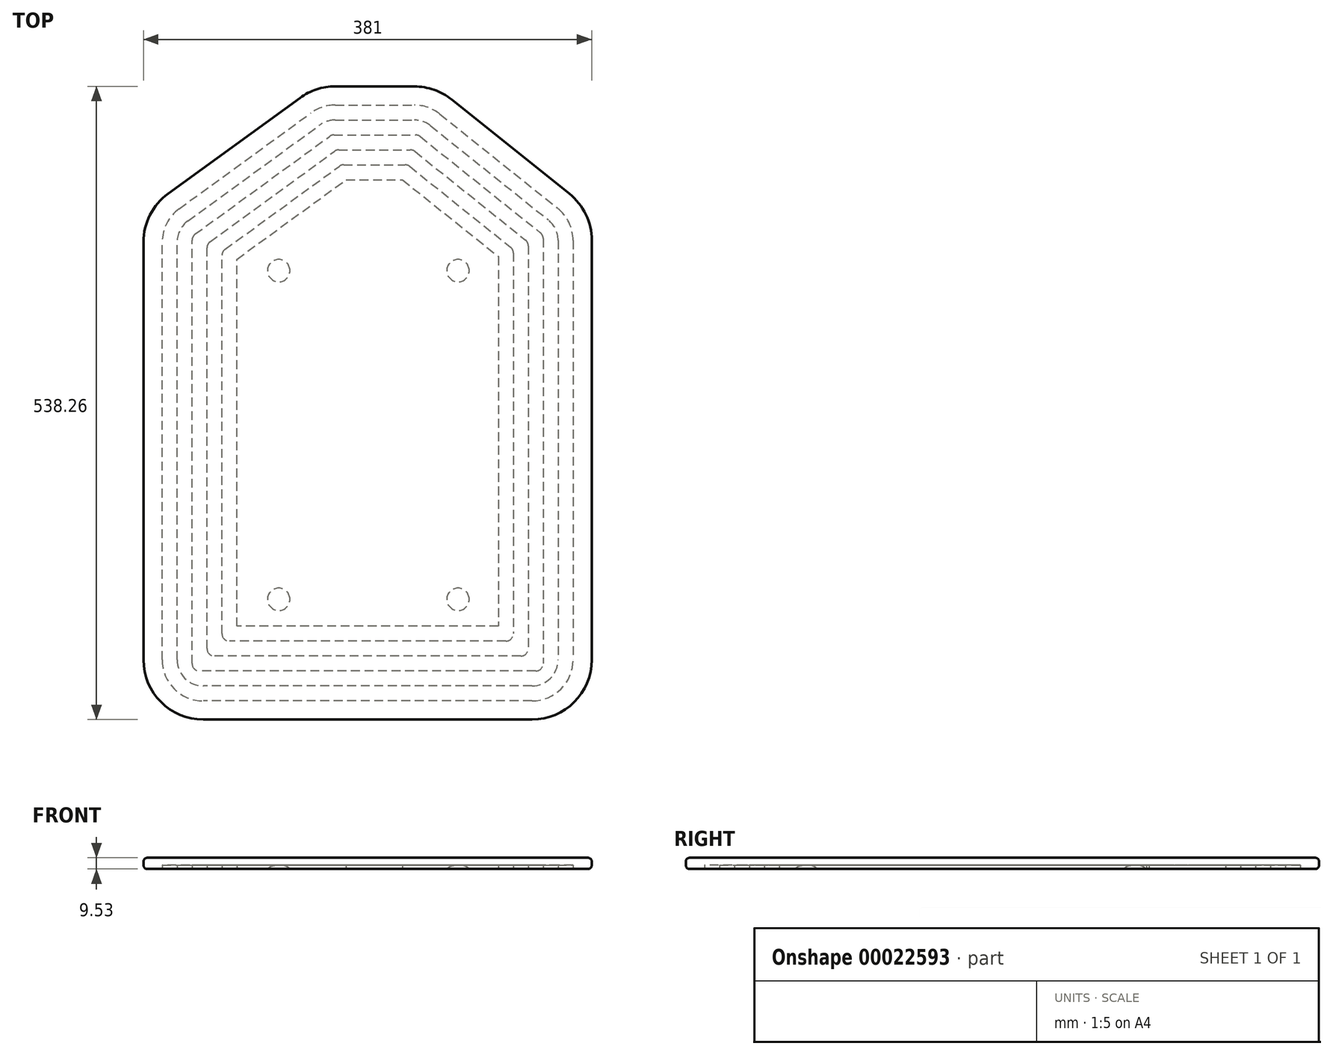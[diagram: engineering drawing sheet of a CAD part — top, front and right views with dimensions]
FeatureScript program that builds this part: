
annotation { "Feature Type Name" : "Feature", "Feature Type Description" : "" }
export const myFeature = defineFeature(function(context is Context, id is Id, definition is map)
    precondition{}
    {
        {
            var Q0;
            Q0=qCreatedBy(makeId("Top.planeOp"),FACE);
            var sketch = newSketch(context, id + "F0", { "sketchPlane" : qUnion([Q0])});
            skLineSegment(sketch, "E0.bottom", {"start": v(138.95, -254.97) * mm, "end": v(-140.45, -254.97) * mm});
            skLineSegment(sketch, "E0.left", {"start": v(189.75, -204.17) * mm, "end": v(189.75, 152.42) * mm});
            skLineSegment(sketch, "E0.right", {"start": v(-191.25, -204.17) * mm, "end": v(-191.25, 150.96) * mm});
            skPoint(sketch, "E0.middle", {"position": v(-0.75, -39.07) * mm});
            skLineSegment(sketch, "E1.bottom", {"start": v(38.9, 283.3) * mm, "end": v(-28.35, 283.3) * mm});
            skPoint(sketch, "E1.middle", {"position": v(-0.75, 176.83) * mm});
            skLineSegment(sketch, "E2", {"start": v(-58.23, 273.57) * mm, "end": v(-170.33, 192.05) * mm});
            skLineSegment(sketch, "E3", {"start": v(170.7, 192.08) * mm, "end": v(70.65, 272.15) * mm});
            skPoint(sketch, "E4.orphan", {"position": v(-58.23, 70.37) * mm});
            skPoint(sketch, "E5.orphan", {"position": v(43.37, 70.37) * mm});
            skPoint(sketch, "E6.visualSharp", {"position": v(-44.87, 283.3) * mm});
            skArc(sketch, "E6.filletArc", {"start": v(-28.35, 283.3) * mm, "mid": v(-44.06, 280.8) * mm, "end": v(-58.23, 273.57) * mm});
            skPoint(sketch, "E7.visualSharp", {"position": v(56.73, 283.3) * mm});
            skArc(sketch, "E7.filletArc", {"start": v(70.65, 272.15) * mm, "mid": v(55.72, 280.43) * mm, "end": v(38.9, 283.3) * mm});
            skPoint(sketch, "E8.visualSharp", {"position": v(189.75, 176.83) * mm});
            skArc(sketch, "E8.filletArc", {"start": v(189.75, 152.42) * mm, "mid": v(184.74, 174.42) * mm, "end": v(170.7, 192.08) * mm});
            skPoint(sketch, "E9.visualSharp", {"position": v(189.75, -254.97) * mm});
            skArc(sketch, "E9.filletArc", {"start": v(138.95, -254.97) * mm, "mid": v(174.87, -240.09) * mm, "end": v(189.75, -204.17) * mm});
            skPoint(sketch, "E10.visualSharp", {"position": v(-191.25, -254.97) * mm});
            skArc(sketch, "E10.filletArc", {"start": v(-191.25, -204.17) * mm, "mid": v(-176.37, -240.09) * mm, "end": v(-140.45, -254.97) * mm});
            skPoint(sketch, "E11.visualSharp", {"position": v(-191.25, 176.83) * mm});
            skArc(sketch, "E11.filletArc", {"start": v(-170.33, 192.05) * mm, "mid": v(-185.72, 174.02) * mm, "end": v(-191.25, 150.96) * mm});
            skSolve(sketch);
        }
        {
            var Q0;
            Q0=makeQuery(id+"F0.imprint","IMPRINT",FACE,{"disambiguationData":[TD([[makeQuery(id+"F0.imprint","IMPRINT",EDGE,{"derivedFrom":sQuery(id+"F0.wireOp",EDGE,"E0.bottom")}),-1.0]])]});
            extrude(context, id + "F1", {"entities" : qUnion([Q0]), "depth" : 9.52 * mm});
        }
        {
            var Q0;
            Q0=makeQuery(id+"F1.opExtrude","CAP_EDGE",EDGE,{"disambiguationData":[OSD([sQuery(id+"F0.wireOp",EDGE,"E10.filletArc")])],"isStart":false});
            var Q1;
            Q1=makeQuery(id+"F1.opExtrude","CAP_EDGE",EDGE,{"disambiguationData":[OSD([sQuery(id+"F0.wireOp",EDGE,"E0.right")])],"isStart":false});
            var Q2;
            Q2=makeQuery(id+"F1.opExtrude","CAP_EDGE",EDGE,{"disambiguationData":[OSD([sQuery(id+"F0.wireOp",EDGE,"E11.filletArc")])],"isStart":false});
            var Q3;
            Q3=makeQuery(id+"F1.opExtrude","CAP_EDGE",EDGE,{"disambiguationData":[OSD([sQuery(id+"F0.wireOp",EDGE,"E2")])],"isStart":false});
            var Q4;
            Q4=makeQuery(id+"F1.opExtrude","CAP_EDGE",EDGE,{"disambiguationData":[OSD([sQuery(id+"F0.wireOp",EDGE,"E1.bottom")])],"isStart":false});
            var Q5;
            Q5=makeQuery(id+"F1.opExtrude","CAP_EDGE",EDGE,{"disambiguationData":[OSD([sQuery(id+"F0.wireOp",EDGE,"E6.filletArc")])],"isStart":false});
            var Q6;
            Q6=makeQuery(id+"F1.opExtrude","CAP_EDGE",EDGE,{"disambiguationData":[OSD([sQuery(id+"F0.wireOp",EDGE,"E3")])],"isStart":false});
            var Q7;
            Q7=makeQuery(id+"F1.opExtrude","CAP_EDGE",EDGE,{"disambiguationData":[OSD([sQuery(id+"F0.wireOp",EDGE,"E7.filletArc")])],"isStart":false});
            var Q8;
            Q8=makeQuery(id+"F1.opExtrude","CAP_EDGE",EDGE,{"disambiguationData":[OSD([sQuery(id+"F0.wireOp",EDGE,"E0.left")])],"isStart":false});
            var Q9;
            Q9=makeQuery(id+"F1.opExtrude","CAP_EDGE",EDGE,{"disambiguationData":[OSD([sQuery(id+"F0.wireOp",EDGE,"E8.filletArc")])],"isStart":false});
            var Q10;
            Q10=makeQuery(id+"F1.opExtrude","CAP_EDGE",EDGE,{"disambiguationData":[OSD([sQuery(id+"F0.wireOp",EDGE,"E9.filletArc")])],"isStart":false});
            var Q11;
            Q11=makeQuery(id+"F1.opExtrude","CAP_EDGE",EDGE,{"disambiguationData":[OSD([sQuery(id+"F0.wireOp",EDGE,"E0.bottom")])],"isStart":false});
            fillet(context, id + "F2", {"entities" : qUnion([Q0, Q1, Q2, Q3, Q4, Q5, Q6, Q7, Q8, Q9, Q10, Q11]), "radius" : 3.17 * mm, "tangentPropagation" : true, "allowEdgeOverflow" : false});
        }
        {
            var Q0;
            Q0=makeQuery(id+"F1.opExtrude","CAP_EDGE",EDGE,{"disambiguationData":[OSD([sQuery(id+"F0.wireOp",EDGE,"E0.bottom")])],"isStart":true});
            var Q1;
            Q1=makeQuery(id+"F1.opExtrude","CAP_EDGE",EDGE,{"disambiguationData":[OSD([sQuery(id+"F0.wireOp",EDGE,"E0.right")])],"isStart":true});
            var Q2;
            Q2=makeQuery(id+"F1.opExtrude","CAP_EDGE",EDGE,{"disambiguationData":[OSD([sQuery(id+"F0.wireOp",EDGE,"E10.filletArc")])],"isStart":true});
            var Q3;
            Q3=makeQuery(id+"F1.opExtrude","CAP_EDGE",EDGE,{"disambiguationData":[OSD([sQuery(id+"F0.wireOp",EDGE,"E9.filletArc")])],"isStart":true});
            var Q4;
            Q4=makeQuery(id+"F1.opExtrude","CAP_EDGE",EDGE,{"disambiguationData":[OSD([sQuery(id+"F0.wireOp",EDGE,"E0.left")])],"isStart":true});
            var Q5;
            Q5=makeQuery(id+"F1.opExtrude","CAP_EDGE",EDGE,{"disambiguationData":[OSD([sQuery(id+"F0.wireOp",EDGE,"E8.filletArc")])],"isStart":true});
            var Q6;
            Q6=makeQuery(id+"F1.opExtrude","CAP_EDGE",EDGE,{"disambiguationData":[OSD([sQuery(id+"F0.wireOp",EDGE,"E3")])],"isStart":true});
            var Q7;
            Q7=makeQuery(id+"F1.opExtrude","CAP_EDGE",EDGE,{"disambiguationData":[OSD([sQuery(id+"F0.wireOp",EDGE,"E7.filletArc")])],"isStart":true});
            var Q8;
            Q8=makeQuery(id+"F1.opExtrude","CAP_EDGE",EDGE,{"disambiguationData":[OSD([sQuery(id+"F0.wireOp",EDGE,"E1.bottom")])],"isStart":true});
            var Q9;
            Q9=makeQuery(id+"F1.opExtrude","CAP_EDGE",EDGE,{"disambiguationData":[OSD([sQuery(id+"F0.wireOp",EDGE,"E6.filletArc")])],"isStart":true});
            var Q10;
            Q10=makeQuery(id+"F1.opExtrude","CAP_EDGE",EDGE,{"disambiguationData":[OSD([sQuery(id+"F0.wireOp",EDGE,"E2")])],"isStart":true});
            var Q11;
            Q11=makeQuery(id+"F1.opExtrude","CAP_EDGE",EDGE,{"disambiguationData":[OSD([sQuery(id+"F0.wireOp",EDGE,"E11.filletArc")])],"isStart":true});
            fillet(context, id + "F3", {"entities" : qUnion([Q0, Q1, Q2, Q3, Q4, Q5, Q6, Q7, Q8, Q9, Q10, Q11]), "radius" : 3.17 * mm, "tangentPropagation" : true, "allowEdgeOverflow" : false});
        }
        {
            var Q0;
            Q0=makeQuery(id+"F1.opExtrude","CAP_FACE",FACE,{"disambiguationData":[OSD([sQuery(id+"F0.wireOp",EDGE,"E0.bottom"),sQuery(id+"F0.wireOp",EDGE,"E0.left"),sQuery(id+"F0.wireOp",EDGE,"E0.right"),sQuery(id+"F0.wireOp",EDGE,"E1.bottom"),sQuery(id+"F0.wireOp",EDGE,"E2"),sQuery(id+"F0.wireOp",EDGE,"E3"),sQuery(id+"F0.wireOp",EDGE,"E6.filletArc"),sQuery(id+"F0.wireOp",EDGE,"E7.filletArc"),sQuery(id+"F0.wireOp",EDGE,"E8.filletArc"),sQuery(id+"F0.wireOp",EDGE,"E9.filletArc"),sQuery(id+"F0.wireOp",EDGE,"E10.filletArc"),sQuery(id+"F0.wireOp",EDGE,"E11.filletArc")])],"isStart":true});
            var sketch = newSketch(context, id + "F4", { "sketchPlane" : qUnion([Q0])});
            skArc(sketch, "E12.0", {"start": v(38.9, -267.42) * mm, "mid": v(50.47, -265.45) * mm, "end": v(60.73, -259.76) * mm});
            skLineSegment(sketch, "E12.1", {"start": v(138.95, 239.1) * mm, "end": v(-140.45, 239.1) * mm});
            skArc(sketch, "E12.2", {"start": v(173.87, 204.17) * mm, "mid": v(163.65, 228.86) * mm, "end": v(138.95, 239.1) * mm});
            skLineSegment(sketch, "E12.3", {"start": v(173.87, -152.42) * mm, "end": v(173.87, 204.17) * mm});
            skArc(sketch, "E12.4", {"start": v(160.77, -179.7) * mm, "mid": v(170.43, -167.55) * mm, "end": v(173.87, -152.42) * mm});
            skArc(sketch, "E12.5", {"start": v(-140.45, 239.1) * mm, "mid": v(-165.15, 228.86) * mm, "end": v(-175.38, 204.17) * mm});
            skLineSegment(sketch, "E12.6", {"start": v(60.73, -259.76) * mm, "end": v(160.77, -179.7) * mm});
            skLineSegment(sketch, "E12.7", {"start": v(-175.38, 204.17) * mm, "end": v(-175.38, -150.96) * mm});
            skArc(sketch, "E12.8", {"start": v(-175.38, -150.96) * mm, "mid": v(-171.57, -166.81) * mm, "end": v(-161, -179.2) * mm});
            skLineSegment(sketch, "E12.9", {"start": v(-161, -179.2) * mm, "end": v(-48.9, -260.74) * mm});
            skArc(sketch, "E12.10", {"start": v(-48.9, -260.74) * mm, "mid": v(-39.15, -265.7) * mm, "end": v(-28.35, -267.42) * mm});
            skLineSegment(sketch, "E12.11", {"start": v(-28.35, -267.42) * mm, "end": v(38.9, -267.42) * mm});
            skLineSegment(sketch, "E13.0", {"start": v(138.95, 226.4) * mm, "end": v(-140.45, 226.4) * mm});
            skArc(sketch, "E13.1", {"start": v(-41.42, -250.46) * mm, "mid": v(-35.22, -253.63) * mm, "end": v(-28.35, -254.72) * mm});
            skLineSegment(sketch, "E13.2", {"start": v(-153.52, -168.94) * mm, "end": v(-41.42, -250.46) * mm});
            skArc(sketch, "E13.3", {"start": v(-162.68, -150.96) * mm, "mid": v(-160.26, -161.05) * mm, "end": v(-153.52, -168.94) * mm});
            skLineSegment(sketch, "E13.4", {"start": v(-162.68, 204.17) * mm, "end": v(-162.68, -150.96) * mm});
            skLineSegment(sketch, "E13.5", {"start": v(-28.35, -254.72) * mm, "end": v(38.9, -254.72) * mm});
            skArc(sketch, "E13.6", {"start": v(-140.45, 226.4) * mm, "mid": v(-156.17, 219.88) * mm, "end": v(-162.68, 204.17) * mm});
            skArc(sketch, "E13.7", {"start": v(38.9, -254.72) * mm, "mid": v(46.26, -253.46) * mm, "end": v(52.8, -249.84) * mm});
            skLineSegment(sketch, "E13.8", {"start": v(52.8, -249.84) * mm, "end": v(152.84, -169.77) * mm});
            skArc(sketch, "E13.9", {"start": v(152.84, -169.77) * mm, "mid": v(158.98, -162.05) * mm, "end": v(161.17, -152.42) * mm});
            skLineSegment(sketch, "E13.10", {"start": v(161.17, -152.42) * mm, "end": v(161.17, 204.17) * mm});
            skArc(sketch, "E13.11", {"start": v(161.17, 204.17) * mm, "mid": v(154.67, 219.88) * mm, "end": v(138.95, 226.4) * mm});
            skLineSegment(sketch, "E14.0", {"start": v(148.47, -153.95) * mm, "end": v(148.47, 207.34) * mm});
            skLineSegment(sketch, "E14.1", {"start": v(-149.98, 207.34) * mm, "end": v(-149.98, -152.58) * mm});
            skLineSegment(sketch, "E14.2", {"start": v(-147.36, -157.72) * mm, "end": v(-33.12, -240.8) * mm});
            skLineSegment(sketch, "E14.3", {"start": v(142.12, 213.7) * mm, "end": v(-143.63, 213.7) * mm});
            skLineSegment(sketch, "E14.4", {"start": v(-29.38, -242.02) * mm, "end": v(40.02, -242.02) * mm});
            skLineSegment(sketch, "E14.5", {"start": v(43.99, -240.62) * mm, "end": v(146.1, -158.9) * mm});
            skLineSegment(sketch, "E15.0", {"start": v(135.77, -147.85) * mm, "end": v(135.77, 194.64) * mm});
            skLineSegment(sketch, "E15.1", {"start": v(-137.28, 194.64) * mm, "end": v(-137.28, -146.11) * mm});
            skLineSegment(sketch, "E15.2", {"start": v(-134.66, -151.25) * mm, "end": v(-28.99, -228.1) * mm});
            skLineSegment(sketch, "E15.3", {"start": v(129.42, 201) * mm, "end": v(-130.93, 201) * mm});
            skLineSegment(sketch, "E15.4", {"start": v(-25.25, -229.32) * mm, "end": v(35.56, -229.32) * mm});
            skLineSegment(sketch, "E15.5", {"start": v(39.53, -227.92) * mm, "end": v(133.4, -152.8) * mm});
            skLineSegment(sketch, "E16.0", {"start": v(116.72, 188.3) * mm, "end": v(-118.23, 188.3) * mm});
            skLineSegment(sketch, "E16.1", {"start": v(-121.96, -144.78) * mm, "end": v(-24.86, -215.4) * mm});
            skLineSegment(sketch, "E16.2", {"start": v(-21.12, -216.62) * mm, "end": v(31.1, -216.62) * mm});
            skLineSegment(sketch, "E16.3", {"start": v(-124.58, 181.94) * mm, "end": v(-124.58, -139.65) * mm});
            skLineSegment(sketch, "E16.4", {"start": v(35.07, -215.22) * mm, "end": v(120.7, -146.7) * mm});
            skLineSegment(sketch, "E16.5", {"start": v(123.07, -141.74) * mm, "end": v(123.07, 181.94) * mm});
            skLineSegment(sketch, "E17.bottom", {"start": v(95.6, -133.68) * mm, "end": v(-94.9, -133.68) * mm});
            skLineSegment(sketch, "E17.top", {"start": v(95.6, 158.42) * mm, "end": v(-94.9, 158.42) * mm});
            skLineSegment(sketch, "E17.left", {"start": v(95.6, -133.68) * mm, "end": v(95.6, 158.42) * mm});
            skLineSegment(sketch, "E17.right", {"start": v(-94.9, -133.68) * mm, "end": v(-94.9, 158.42) * mm});
            skPoint(sketch, "E17.middle", {"position": v(0.35, 12.37) * mm});
            skPoint(sketch, "E18.visualSharp", {"position": v(-137.28, 201) * mm});
            skArc(sketch, "E18.filletArc", {"start": v(-130.93, 201) * mm, "mid": v(-135.42, 199.13) * mm, "end": v(-137.28, 194.64) * mm});
            skPoint(sketch, "E19.visualSharp", {"position": v(-149.98, 213.7) * mm});
            skArc(sketch, "E19.filletArc", {"start": v(-143.63, 213.7) * mm, "mid": v(-148.12, 211.83) * mm, "end": v(-149.98, 207.34) * mm});
            skPoint(sketch, "E20.visualSharp", {"position": v(-124.58, 188.3) * mm});
            skArc(sketch, "E20.filletArc", {"start": v(-118.23, 188.3) * mm, "mid": v(-122.72, 186.43) * mm, "end": v(-124.58, 181.94) * mm});
            skPoint(sketch, "E21.visualSharp", {"position": v(148.47, 213.7) * mm});
            skArc(sketch, "E21.filletArc", {"start": v(148.47, 207.34) * mm, "mid": v(146.61, 211.83) * mm, "end": v(142.12, 213.7) * mm});
            skPoint(sketch, "E22.visualSharp", {"position": v(135.77, 201) * mm});
            skArc(sketch, "E22.filletArc", {"start": v(135.77, 194.64) * mm, "mid": v(133.91, 199.13) * mm, "end": v(129.42, 201) * mm});
            skPoint(sketch, "E23.visualSharp", {"position": v(123.07, 188.3) * mm});
            skArc(sketch, "E23.filletArc", {"start": v(123.07, 181.94) * mm, "mid": v(121.21, 186.43) * mm, "end": v(116.72, 188.3) * mm});
            skPoint(sketch, "E24.visualSharp", {"position": v(-149.98, -155.81) * mm});
            skArc(sketch, "E24.filletArc", {"start": v(-149.98, -152.58) * mm, "mid": v(-149.28, -155.46) * mm, "end": v(-147.36, -157.72) * mm});
            skPoint(sketch, "E25.visualSharp", {"position": v(-137.28, -149.35) * mm});
            skArc(sketch, "E25.filletArc", {"start": v(-137.28, -146.11) * mm, "mid": v(-136.58, -149) * mm, "end": v(-134.66, -151.25) * mm});
            skPoint(sketch, "E26.visualSharp", {"position": v(-124.58, -142.88) * mm});
            skArc(sketch, "E26.filletArc", {"start": v(-124.58, -139.65) * mm, "mid": v(-123.88, -142.53) * mm, "end": v(-121.96, -144.78) * mm});
            skPoint(sketch, "E27.visualSharp", {"position": v(148.47, -157) * mm});
            skArc(sketch, "E27.filletArc", {"start": v(146.1, -158.9) * mm, "mid": v(147.85, -156.7) * mm, "end": v(148.47, -153.95) * mm});
            skPoint(sketch, "E28.visualSharp", {"position": v(135.77, -150.9) * mm});
            skArc(sketch, "E28.filletArc", {"start": v(133.4, -152.8) * mm, "mid": v(135.15, -150.6) * mm, "end": v(135.77, -147.85) * mm});
            skPoint(sketch, "E29.visualSharp", {"position": v(123.07, -144.8) * mm});
            skArc(sketch, "E29.filletArc", {"start": v(120.7, -146.7) * mm, "mid": v(122.45, -144.5) * mm, "end": v(123.07, -141.74) * mm});
            skPoint(sketch, "E30.visualSharp", {"position": v(-31.45, -242.02) * mm});
            skArc(sketch, "E30.filletArc", {"start": v(-33.12, -240.8) * mm, "mid": v(-31.35, -241.7) * mm, "end": v(-29.38, -242.02) * mm});
            skPoint(sketch, "E31.visualSharp", {"position": v(42.25, -242.02) * mm});
            skArc(sketch, "E31.filletArc", {"start": v(40.02, -242.02) * mm, "mid": v(42.12, -241.66) * mm, "end": v(43.99, -240.62) * mm});
            skPoint(sketch, "E32.visualSharp", {"position": v(37.8, -229.32) * mm});
            skArc(sketch, "E32.filletArc", {"start": v(35.56, -229.32) * mm, "mid": v(37.66, -228.96) * mm, "end": v(39.53, -227.92) * mm});
            skPoint(sketch, "E33.visualSharp", {"position": v(33.33, -216.62) * mm});
            skArc(sketch, "E33.filletArc", {"start": v(31.1, -216.62) * mm, "mid": v(33.2, -216.26) * mm, "end": v(35.07, -215.22) * mm});
            skPoint(sketch, "E34.visualSharp", {"position": v(-23.19, -216.62) * mm});
            skArc(sketch, "E34.filletArc", {"start": v(-24.86, -215.4) * mm, "mid": v(-23.09, -216.3) * mm, "end": v(-21.12, -216.62) * mm});
            skPoint(sketch, "E35.visualSharp", {"position": v(-27.32, -229.32) * mm});
            skArc(sketch, "E35.filletArc", {"start": v(-28.99, -228.1) * mm, "mid": v(-27.22, -229) * mm, "end": v(-25.25, -229.32) * mm});
            skLineSegment(sketch, "E36.0", {"start": v(110.37, -138.7) * mm, "end": v(110.37, 175.6) * mm});
            skLineSegment(sketch, "E36.1", {"start": v(-111.88, 175.6) * mm, "end": v(-111.88, -136.41) * mm});
            skLineSegment(sketch, "E36.2", {"start": v(-111.88, -136.41) * mm, "end": v(-19.06, -203.92) * mm});
            skLineSegment(sketch, "E36.3", {"start": v(110.37, 175.6) * mm, "end": v(-111.88, 175.6) * mm});
            skLineSegment(sketch, "E36.4", {"start": v(-19.06, -203.92) * mm, "end": v(28.88, -203.92) * mm});
            skLineSegment(sketch, "E36.5", {"start": v(28.88, -203.92) * mm, "end": v(110.37, -138.7) * mm});
            skSolve(sketch);
        }
        {
            var Q0;
            Q0=makeQuery(id+"F4.imprint","IMPRINT",FACE,{"disambiguationData":[TD([[makeQuery(id+"F4.imprint","IMPRINT",EDGE,{"derivedFrom":sQuery(id+"F4.wireOp",EDGE,"E12.0")}),1.0]])]});
            var Q1;
            Q1=makeQuery(id+"F4.imprint","IMPRINT",FACE,{"disambiguationData":[TD([[makeQuery(id+"F4.imprint","IMPRINT",EDGE,{"derivedFrom":sQuery(id+"F4.wireOp",EDGE,"E14.0")}),1.0]])]});
            var Q2;
            Q2=makeQuery(id+"F4.imprint","IMPRINT",FACE,{"disambiguationData":[TD([[makeQuery(id+"F4.imprint","IMPRINT",EDGE,{"derivedFrom":sQuery(id+"F4.wireOp",EDGE,"E16.0")}),1.0]])]});
            extrude(context, id + "F5", {"entities" : qUnion([Q0, Q1, Q2]), "operationType" : NewBodyOperationType.REMOVE, "oppositeDirection" : true, "depth" : 3.17 * mm});
        }
        {
            var Q0;
            Q0=makeQuery(id+"F5.boolean.opBoolean","SPLIT",FACE,{"disambiguationData":[TD([makeQuery(id+"F5.opExtrude","SWEPT_FACE",FACE,{"disambiguationData":[OSD([sQuery(id+"F4.wireOp",EDGE,"E36.0")])]})])],"derivedFrom":makeQuery(id+"F1.opExtrude","CAP_FACE",FACE,{"disambiguationData":[OSD([sQuery(id+"F0.wireOp",EDGE,"E0.bottom"),sQuery(id+"F0.wireOp",EDGE,"E0.left"),sQuery(id+"F0.wireOp",EDGE,"E0.right"),sQuery(id+"F0.wireOp",EDGE,"E1.bottom"),sQuery(id+"F0.wireOp",EDGE,"E2"),sQuery(id+"F0.wireOp",EDGE,"E3"),sQuery(id+"F0.wireOp",EDGE,"E6.filletArc"),sQuery(id+"F0.wireOp",EDGE,"E7.filletArc"),sQuery(id+"F0.wireOp",EDGE,"E8.filletArc"),sQuery(id+"F0.wireOp",EDGE,"E9.filletArc"),sQuery(id+"F0.wireOp",EDGE,"E10.filletArc"),sQuery(id+"F0.wireOp",EDGE,"E11.filletArc")])],"isStart":true})});
            var sketch = newSketch(context, id + "F6", { "sketchPlane" : qUnion([Q0])});
            skLineSegment(sketch, "E37.bottom", {"start": v(76.08, -126.67) * mm, "end": v(-76.32, -126.67) * mm});
            skLineSegment(sketch, "E37.top", {"start": v(76.08, 152.73) * mm, "end": v(-76.32, 152.73) * mm});
            skLineSegment(sketch, "E37.left", {"start": v(76.08, -126.67) * mm, "end": v(76.08, 152.73) * mm});
            skLineSegment(sketch, "E37.right", {"start": v(-76.32, -126.67) * mm, "end": v(-76.32, 152.73) * mm});
            skPoint(sketch, "E37.middle", {"position": v(-0.12, 13.03) * mm});
            skCircle(sketch, "E38", {"center": v(-76.32, 152.73) * mm, "radius": 9.53 * mm});
            skCircle(sketch, "E39", {"center": v(76.08, 152.73) * mm, "radius": 9.53 * mm});
            skCircle(sketch, "E40", {"center": v(-76.32, -126.67) * mm, "radius": 9.53 * mm});
            skCircle(sketch, "E41", {"center": v(76.08, -126.67) * mm, "radius": 9.53 * mm});
            skSolve(sketch);
        }
        {
            var Q0;
            {var subQ0=sQuery(id+"F6.wireOp",EDGE,"E37.right");var subQ1=sQuery(id+"F6.wireOp",EDGE,"E37.top");var subQ2=makeQuery(id+"F6.imprint","INTERSECT",VERTEX,{"derivedFrom":[subQ1,subQ0]});Q0=makeQuery(id+"F6.imprint","IMPRINT",FACE,{"disambiguationData":[TD([[makeQuery(id+"F6.imprint","IMPRINT",EDGE,{"disambiguationData":[TD([[subQ2,1.0]])],"derivedFrom":subQ1}),-1.0]])]});}
            var Q1;
            {var subQ0=sQuery(id+"F6.wireOp",EDGE,"E37.right");var subQ1=sQuery(id+"F6.wireOp",EDGE,"E37.top");var subQ2=makeQuery(id+"F6.imprint","INTERSECT",VERTEX,{"derivedFrom":[subQ1,subQ0]});Q1=makeQuery(id+"F6.imprint","IMPRINT",FACE,{"disambiguationData":[TD([[makeQuery(id+"F6.imprint","IMPRINT",EDGE,{"disambiguationData":[TD([[subQ2,1.0]])],"derivedFrom":subQ1}),1.0]])]});}
            var Q2;
            {var subQ0=sQuery(id+"F6.wireOp",EDGE,"E37.left");var subQ1=sQuery(id+"F6.wireOp",EDGE,"E37.top");var subQ2=makeQuery(id+"F6.imprint","INTERSECT",VERTEX,{"derivedFrom":[subQ1,subQ0]});Q2=makeQuery(id+"F6.imprint","IMPRINT",FACE,{"disambiguationData":[TD([[makeQuery(id+"F6.imprint","IMPRINT",EDGE,{"disambiguationData":[TD([[subQ2,-1.0]])],"derivedFrom":subQ1}),-1.0]])]});}
            var Q3;
            {var subQ0=sQuery(id+"F6.wireOp",EDGE,"E37.left");var subQ1=sQuery(id+"F6.wireOp",EDGE,"E37.top");var subQ2=makeQuery(id+"F6.imprint","INTERSECT",VERTEX,{"derivedFrom":[subQ1,subQ0]});Q3=makeQuery(id+"F6.imprint","IMPRINT",FACE,{"disambiguationData":[TD([[makeQuery(id+"F6.imprint","IMPRINT",EDGE,{"disambiguationData":[TD([[subQ2,-1.0]])],"derivedFrom":subQ1}),1.0]])]});}
            var Q4;
            {var subQ0=sQuery(id+"F6.wireOp",EDGE,"E37.left");var subQ1=sQuery(id+"F6.wireOp",EDGE,"E37.bottom");var subQ2=makeQuery(id+"F6.imprint","INTERSECT",VERTEX,{"derivedFrom":[subQ1,subQ0]});Q4=makeQuery(id+"F6.imprint","IMPRINT",FACE,{"disambiguationData":[TD([[makeQuery(id+"F6.imprint","IMPRINT",EDGE,{"disambiguationData":[TD([[subQ2,-1.0]])],"derivedFrom":subQ1}),-1.0]])]});}
            var Q5;
            {var subQ0=sQuery(id+"F6.wireOp",EDGE,"E37.left");var subQ1=sQuery(id+"F6.wireOp",EDGE,"E37.bottom");var subQ2=makeQuery(id+"F6.imprint","INTERSECT",VERTEX,{"derivedFrom":[subQ1,subQ0]});Q5=makeQuery(id+"F6.imprint","IMPRINT",FACE,{"disambiguationData":[TD([[makeQuery(id+"F6.imprint","IMPRINT",EDGE,{"disambiguationData":[TD([[subQ2,-1.0]])],"derivedFrom":subQ1}),1.0]])]});}
            var Q6;
            {var subQ0=sQuery(id+"F6.wireOp",EDGE,"E37.right");var subQ1=sQuery(id+"F6.wireOp",EDGE,"E37.bottom");var subQ2=makeQuery(id+"F6.imprint","INTERSECT",VERTEX,{"derivedFrom":[subQ1,subQ0]});Q6=makeQuery(id+"F6.imprint","IMPRINT",FACE,{"disambiguationData":[TD([[makeQuery(id+"F6.imprint","IMPRINT",EDGE,{"disambiguationData":[TD([[subQ2,1.0]])],"derivedFrom":subQ1}),-1.0]])]});}
            var Q7;
            {var subQ0=sQuery(id+"F6.wireOp",EDGE,"E37.right");var subQ1=sQuery(id+"F6.wireOp",EDGE,"E37.bottom");var subQ2=makeQuery(id+"F6.imprint","INTERSECT",VERTEX,{"derivedFrom":[subQ1,subQ0]});Q7=makeQuery(id+"F6.imprint","IMPRINT",FACE,{"disambiguationData":[TD([[makeQuery(id+"F6.imprint","IMPRINT",EDGE,{"disambiguationData":[TD([[subQ2,1.0]])],"derivedFrom":subQ1}),1.0]])]});}
            var Q8;
            Q8=sQuery(id+"F6.wireOp",EDGE,"E38");
            var Q9;
            Q9=sQuery(id+"F6.wireOp",EDGE,"E39");
            var Q10;
            Q10=sQuery(id+"F6.wireOp",EDGE,"E40");
            var Q11;
            Q11=sQuery(id+"F6.wireOp",EDGE,"E41");
            extrude(context, id + "F7", {"entities" : qUnion([Q0, Q1, Q2, Q3, Q4, Q5, Q6, Q7]), "operationType" : NewBodyOperationType.REMOVE, "surfaceEntities" : qUnion([Q8, Q9, Q10, Q11]), "oppositeDirection" : true, "depth" : 3.17 * mm});
        }
        {
            var Q0;
            Q0=makeQuery(id+"F7.boolean.opBoolean","COPY",EDGE,{"derivedFrom":makeQuery(id+"F7.opExtrude","CAP_EDGE",EDGE,{"disambiguationData":[OSD([sQuery(id+"F6.wireOp",EDGE,"E39")])],"isStart":false})});
            var Q1;
            Q1=makeQuery(id+"F7.boolean.opBoolean","COPY",EDGE,{"derivedFrom":makeQuery(id+"F7.opExtrude","CAP_EDGE",EDGE,{"disambiguationData":[OSD([sQuery(id+"F6.wireOp",EDGE,"E38")])],"isStart":false})});
            var Q2;
            Q2=makeQuery(id+"F7.boolean.opBoolean","COPY",FACE,{"derivedFrom":makeQuery(id+"F7.opExtrude","CAP_FACE",FACE,{"disambiguationData":[OSD([sQuery(id+"F6.wireOp",EDGE,"E41")])],"isStart":false})});
            var Q3;
            Q3=makeQuery(id+"F7.boolean.opBoolean","COPY",FACE,{"derivedFrom":makeQuery(id+"F7.opExtrude","CAP_FACE",FACE,{"disambiguationData":[OSD([sQuery(id+"F6.wireOp",EDGE,"E40")])],"isStart":false})});
            fillet(context, id + "F8", {"entities" : qUnion([Q0, Q1, Q2, Q3]), "radius" : 9.52 * mm, "tangentPropagation" : true, "allowEdgeOverflow" : false});
        }
    });
